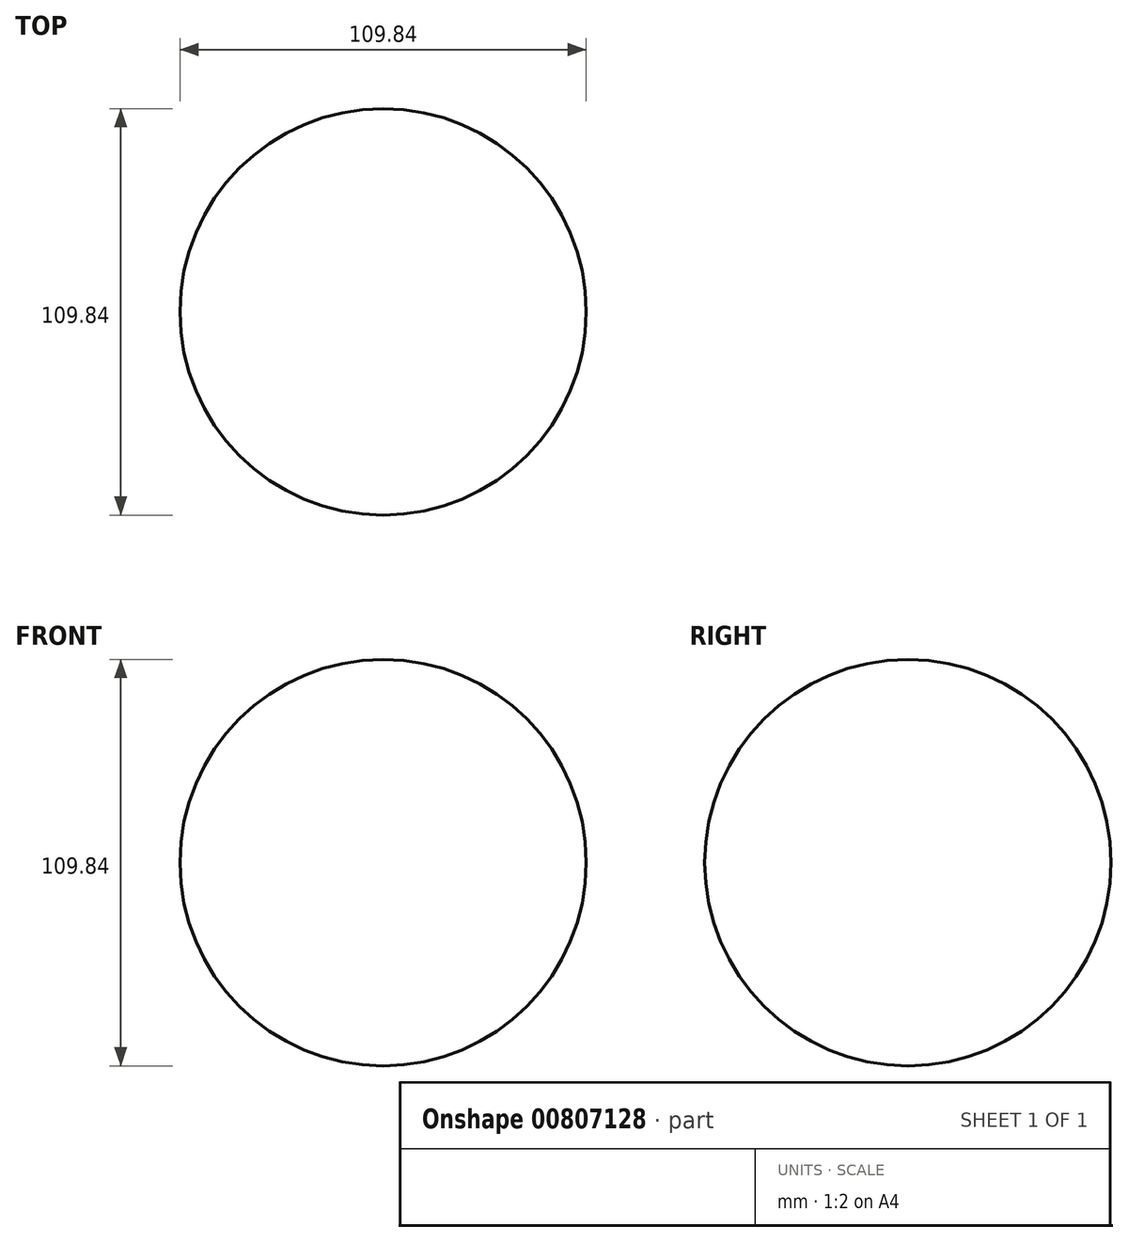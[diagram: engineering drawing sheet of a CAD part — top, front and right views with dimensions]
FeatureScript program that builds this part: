
annotation { "Feature Type Name" : "Feature", "Feature Type Description" : "" }
export const myFeature = defineFeature(function(context is Context, id is Id, definition is map)
    precondition{}
    {
        {
            var Q0;
            Q0=qCreatedBy(makeId("Front.planeOp"),FACE);
            var sketch = newSketch(context, id + "F0", { "sketchPlane" : qUnion([Q0])});
            skCircle(sketch, "E0", {"center": v(0, 0) * mm, "radius": 54.92 * mm});
            skLineSegment(sketch, "E1", {"start": v(61.66, 0) * mm, "end": v(-63.48, 0) * mm});
            skSolve(sketch);
        }
        {
            var Q0;
            {var subQ0=sQuery(id+"F0.wireOp",EDGE,"E1");var subQ1=sQuery(id+"F0.wireOp",EDGE,"E0");var subQ2=makeQuery(id+"F0.imprint","INTERSECT",VERTEX,{"disambiguationData":[OD(0.0)],"derivedFrom":[subQ1,subQ0]});Q0=makeQuery(id+"F0.imprint","IMPRINT",FACE,{"disambiguationData":[TD([[makeQuery(id+"F0.imprint","IMPRINT",EDGE,{"disambiguationData":[TD([[subQ2,-1.0]])],"derivedFrom":subQ1}),1.0]])]});}
            var Q1;
            Q1=sQuery(id+"F0.wireOp",EDGE,"E1");
            revolve(context, id + "F1", {"surfaceOperationType" : NewSurfaceOperationType.NEW, "entities" : qUnion([Q0]), "axis" : qUnion([Q1]), "revolveType" : RevolveType.FULL});
        }
    });
